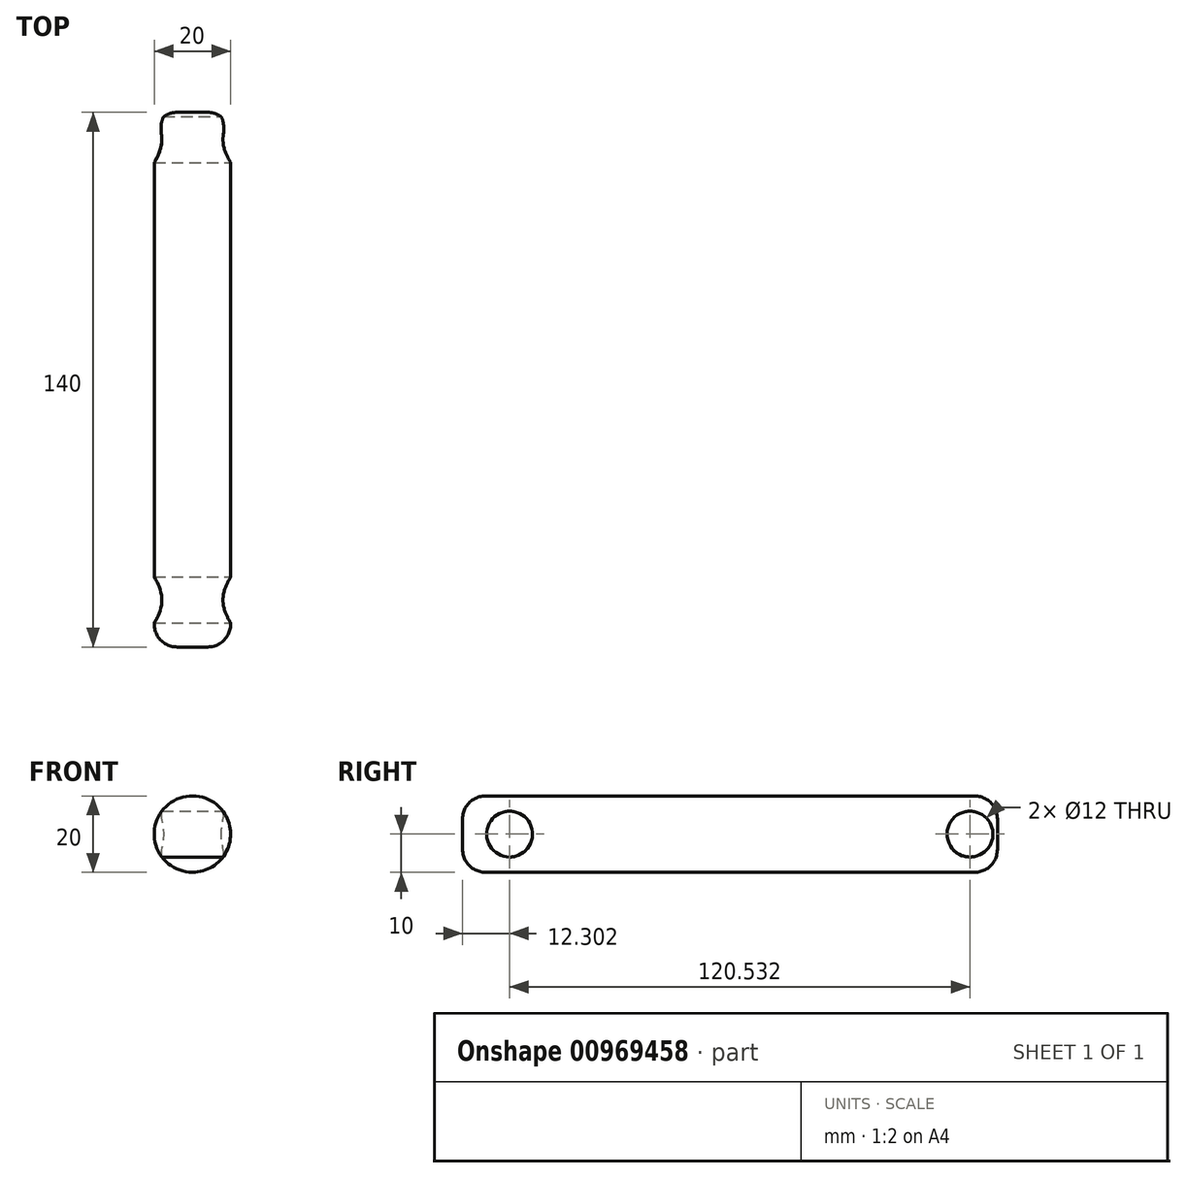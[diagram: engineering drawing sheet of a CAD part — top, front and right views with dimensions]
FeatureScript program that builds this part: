
annotation { "Feature Type Name" : "Feature", "Feature Type Description" : "" }
export const myFeature = defineFeature(function(context is Context, id is Id, definition is map)
    precondition{}
    {
        {
            var Q0;
            Q0=qCreatedBy(makeId("Front.planeOp"),FACE);
            var sketch = newSketch(context, id + "F0", { "sketchPlane" : qUnion([Q0])});
            skCircle(sketch, "E0", {"center": v(0, 0) * mm, "radius": 10 * mm});
            skSolve(sketch);
        }
        {
            var Q0;
            Q0 = qSketchRegion(id + "F0", true);
            extrude(context, id + "F1", {"entities" : qUnion([Q0]), "depth" : 140 * mm, "offsetDistance" : 25 * mm});
        }
        {
            var Q0;
            Q0=qCreatedBy(makeId("Right.planeOp"),FACE);
            var sketch = newSketch(context, id + "F2", { "sketchPlane" : qUnion([Q0])});
            skCircle(sketch, "E1", {"center": v(-7.17, 0) * mm, "radius": 6 * mm});
            skSolve(sketch);
        }
        {
            var Q0;
            Q0 = qSketchRegion(id + "F2", true);
            extrude(context, id + "F3", {"entities" : qUnion([Q0]), "operationType" : NewBodyOperationType.REMOVE, "endBound" : BoundingType.SYMMETRIC, "oppositeDirection" : true, "depth" : 400 * mm, "offsetDistance" : 25 * mm});
        }
        {
            var Q0;
            Q0=makeQuery(id+"F1.opExtrude","CAP_EDGE",EDGE,{"disambiguationData":[OSD([sQuery(id+"F0.wireOp",EDGE,"E0")])],"isStart":true});
            fillet(context, id + "F4", {"entities" : qUnion([Q0]), "radius" : 6 * mm, "tangentPropagation" : true, "allowEdgeOverflow" : false});
        }
        {
            var Q0;
            Q0=qCreatedBy(makeId("Right.planeOp"),FACE);
            var sketch = newSketch(context, id + "F5", { "sketchPlane" : qUnion([Q0])});
            skCircle(sketch, "E2", {"center": v(-127.7, 0) * mm, "radius": 6 * mm});
            skSolve(sketch);
        }
        {
            var Q0;
            Q0 = qSketchRegion(id + "F5", true);
            extrude(context, id + "F6", {"entities" : qUnion([Q0]), "operationType" : NewBodyOperationType.REMOVE, "endBound" : BoundingType.SYMMETRIC, "oppositeDirection" : true, "depth" : 25 * mm, "offsetDistance" : 25 * mm});
        }
        {
            var Q0;
            Q0=makeQuery(id+"F1.opExtrude","CAP_FACE",FACE,{"disambiguationData":[OSD([sQuery(id+"F0.wireOp",EDGE,"E0")])],"isStart":false});
            fillet(context, id + "F7", {"entities" : qUnion([Q0]), "radius" : 6 * mm, "tangentPropagation" : true, "allowEdgeOverflow" : false});
        }
    });
